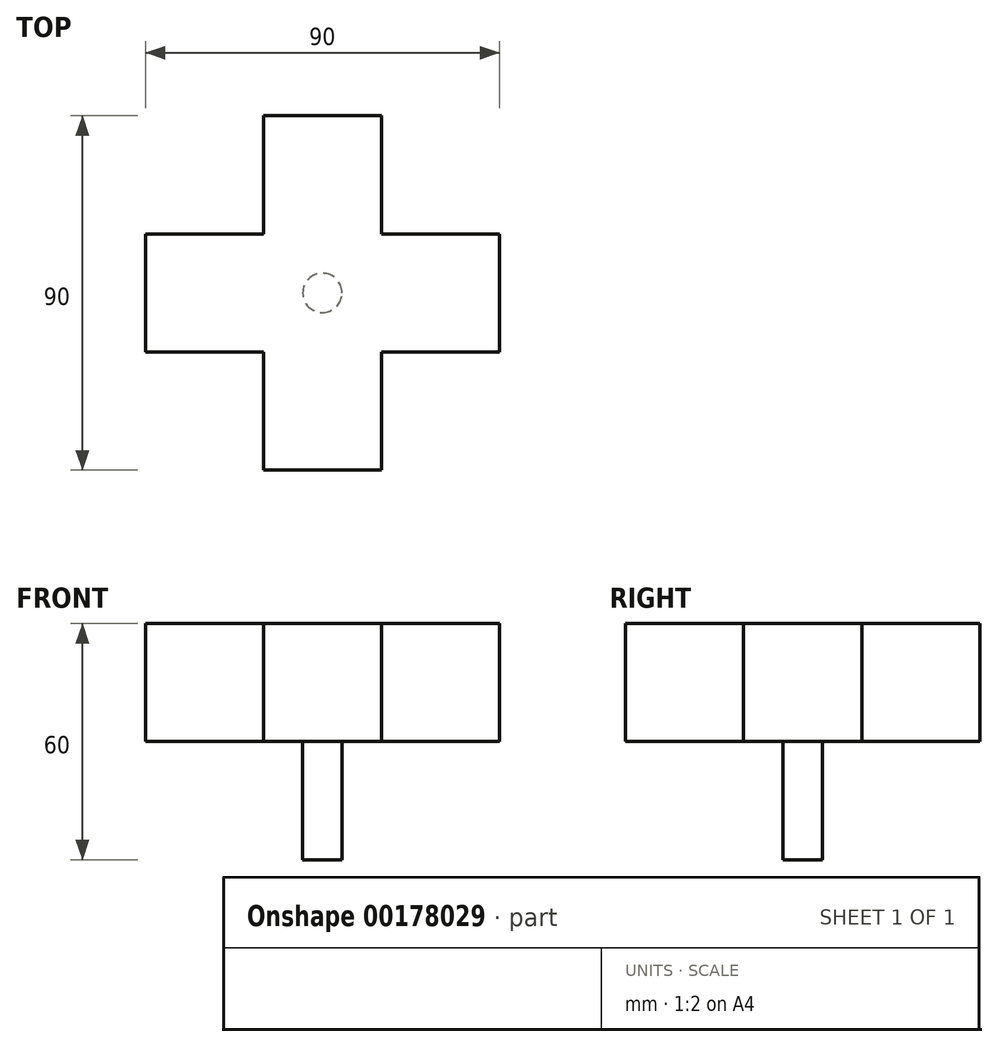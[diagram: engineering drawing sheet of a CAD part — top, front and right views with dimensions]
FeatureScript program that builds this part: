
annotation { "Feature Type Name" : "Feature", "Feature Type Description" : "" }
export const myFeature = defineFeature(function(context is Context, id is Id, definition is map)
    precondition{}
    {
        {
            var Q0;
            Q0=qCreatedBy(makeId("Top.planeOp"),FACE);
            var sketch = newSketch(context, id + "F0", { "sketchPlane" : qUnion([Q0])});
            skLineSegment(sketch, "E0", {"start": v(45, 0) * mm, "end": v(45, 15) * mm});
            skLineSegment(sketch, "E1", {"start": v(45, 15) * mm, "end": v(15, 15) * mm});
            skLineSegment(sketch, "E2", {"start": v(15, 15) * mm, "end": v(15, 45) * mm});
            skLineSegment(sketch, "E3", {"start": v(15, 45) * mm, "end": v(0, 45) * mm});
            skLineSegment(sketch, "E4", {"start": v(0, 45) * mm, "end": v(0, 0) * mm, "construction": true});
            skLineSegment(sketch, "E5.MirrorCS", {"start": v(-15, 45) * mm, "end": v(0, 45) * mm});
            skLineSegment(sketch, "E6.MirrorCS", {"start": v(-15, 15) * mm, "end": v(-15, 45) * mm});
            skLineSegment(sketch, "E7.MirrorCS", {"start": v(-45, 15) * mm, "end": v(-15, 15) * mm});
            skLineSegment(sketch, "E8.MirrorCS", {"start": v(-45, 0) * mm, "end": v(-45, 15) * mm});
            skLineSegment(sketch, "E9", {"start": v(-45, 0) * mm, "end": v(45, 0) * mm, "construction": true});
            skLineSegment(sketch, "E10.MirrorCS", {"start": v(45, 0) * mm, "end": v(45, -15) * mm});
            skLineSegment(sketch, "E11.MirrorCS", {"start": v(-45, 0) * mm, "end": v(-45, -15) * mm});
            skLineSegment(sketch, "E12.MirrorCS", {"start": v(-45, -15) * mm, "end": v(-15, -15) * mm});
            skLineSegment(sketch, "E13.MirrorCS", {"start": v(45, -15) * mm, "end": v(15, -15) * mm});
            skLineSegment(sketch, "E14.MirrorCS", {"start": v(15, -15) * mm, "end": v(15, -45) * mm});
            skLineSegment(sketch, "E15.MirrorCS", {"start": v(-15, -15) * mm, "end": v(-15, -45) * mm});
            skLineSegment(sketch, "E16.MirrorCS", {"start": v(-15, -45) * mm, "end": v(0, -45) * mm});
            skLineSegment(sketch, "E17.MirrorCS", {"start": v(15, -45) * mm, "end": v(0, -45) * mm});
            skSolve(sketch);
        }
        {
            var Q0;
            Q0=makeQuery(id+"F0.imprint","IMPRINT",FACE,{"disambiguationData":[TD([[makeQuery(id+"F0.imprint","IMPRINT",EDGE,{"derivedFrom":sQuery(id+"F0.wireOp",EDGE,"E0")}),1.0]])]});
            extrude(context, id + "F1", {"entities" : qUnion([Q0]), "depth" : 30 * mm});
        }
        {
            var Q0;
            Q0=makeQuery(id+"F1.opExtrude","CAP_FACE",FACE,{"disambiguationData":[OSD([sQuery(id+"F0.wireOp",EDGE,"E0"),sQuery(id+"F0.wireOp",EDGE,"E1"),sQuery(id+"F0.wireOp",EDGE,"E2"),sQuery(id+"F0.wireOp",EDGE,"E3"),sQuery(id+"F0.wireOp",EDGE,"E5.MirrorCS"),sQuery(id+"F0.wireOp",EDGE,"E6.MirrorCS"),sQuery(id+"F0.wireOp",EDGE,"E7.MirrorCS"),sQuery(id+"F0.wireOp",EDGE,"E8.MirrorCS"),sQuery(id+"F0.wireOp",EDGE,"E10.MirrorCS"),sQuery(id+"F0.wireOp",EDGE,"E11.MirrorCS"),sQuery(id+"F0.wireOp",EDGE,"E12.MirrorCS"),sQuery(id+"F0.wireOp",EDGE,"E13.MirrorCS"),sQuery(id+"F0.wireOp",EDGE,"E14.MirrorCS"),sQuery(id+"F0.wireOp",EDGE,"E15.MirrorCS"),sQuery(id+"F0.wireOp",EDGE,"E16.MirrorCS"),sQuery(id+"F0.wireOp",EDGE,"E17.MirrorCS")])],"isStart":true});
            var sketch = newSketch(context, id + "F2", { "sketchPlane" : qUnion([Q0])});
            skCircle(sketch, "E18", {"center": v(0, 0) * mm, "radius": 5 * mm});
            skSolve(sketch);
        }
        {
            var Q0;
            Q0=makeQuery(id+"F2.imprint","IMPRINT",FACE,{"disambiguationData":[TD([[makeQuery(id+"F2.imprint","IMPRINT",EDGE,{"derivedFrom":sQuery(id+"F2.wireOp",EDGE,"E18")}),1.0]])]});
            extrude(context, id + "F3", {"entities" : qUnion([Q0]), "operationType" : NewBodyOperationType.ADD, "depth" : 30 * mm});
        }
    });
